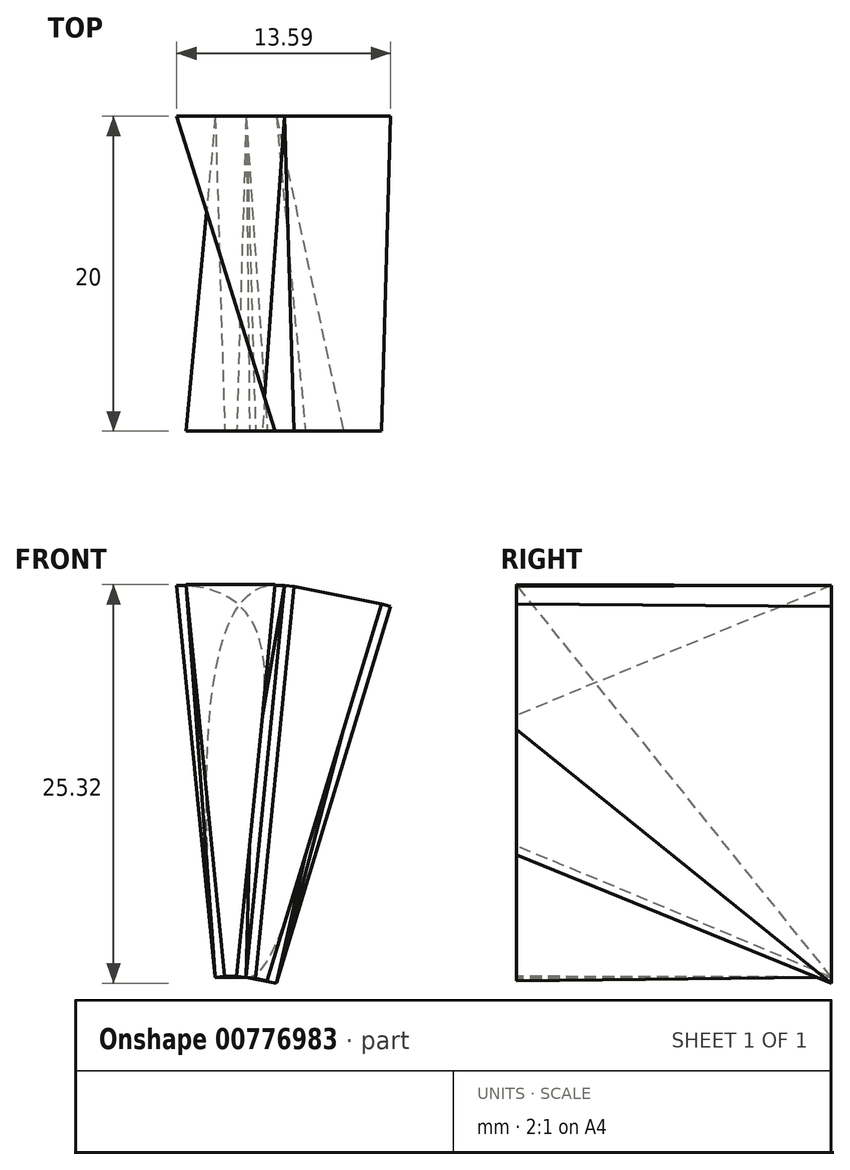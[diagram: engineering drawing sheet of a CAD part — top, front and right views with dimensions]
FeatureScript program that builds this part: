
annotation { "Feature Type Name" : "Feature", "Feature Type Description" : "" }
export const myFeature = defineFeature(function(context is Context, id is Id, definition is map)
    precondition{}
    {
        {
            var Q0;
            Q0=qCreatedBy(makeId("Front.planeOp"),FACE);
            var sketch = newSketch(context, id + "F0", { "sketchPlane" : qUnion([Q0])});
            skCircle(sketch, "E0", {"center": v(0, 0) * mm, "radius": 10 * mm, "construction": true});
            skCircle(sketch, "E1", {"center": v(0, 0) * mm, "radius": 35 * mm, "construction": true});
            skCircle(sketch, "E2", {"center": v(0, 0) * mm, "radius": 49 * mm});
            skLineSegment(sketch, "E3", {"start": v(-0.98, 9.95) * mm, "end": v(0.98, 9.95) * mm});
            skLineSegment(sketch, "E4", {"start": v(0.98, 9.95) * mm, "end": v(3.43, 34.83) * mm});
            skLineSegment(sketch, "E5", {"start": v(3.43, 34.83) * mm, "end": v(-3.43, 34.83) * mm});
            skLineSegment(sketch, "E6", {"start": v(-3.43, 34.83) * mm, "end": v(-0.98, 9.95) * mm});
            skLineSegment(sketch, "E7", {"start": v(0, 0) * mm, "end": v(-4.8, 48.76) * mm, "construction": true});
            skLineSegment(sketch, "E8", {"start": v(-4.8, 48.76) * mm, "end": v(0, 0) * mm, "construction": true});
            skLineSegment(sketch, "E9", {"start": v(0, 0) * mm, "end": v(4.8, 48.76) * mm, "construction": true});
            skLineSegment(sketch, "E10.1.0", {"start": v(-10.16, 33.5) * mm, "end": v(-2.9, 9.57) * mm});
            skLineSegment(sketch, "E10.1.1", {"start": v(-3.43, 34.83) * mm, "end": v(-10.16, 33.5) * mm});
            skLineSegment(sketch, "E10.1.2", {"start": v(-0.98, 9.95) * mm, "end": v(-3.43, 34.83) * mm});
            skLineSegment(sketch, "E10.1.3", {"start": v(-2.9, 9.57) * mm, "end": v(-0.98, 9.95) * mm});
            skLineSegment(sketch, "E10.2.0", {"start": v(-16.5, 30.87) * mm, "end": v(-4.72, 8.82) * mm});
            skLineSegment(sketch, "E10.2.1", {"start": v(-10.16, 33.5) * mm, "end": v(-16.5, 30.87) * mm});
            skLineSegment(sketch, "E10.2.2", {"start": v(-2.9, 9.57) * mm, "end": v(-10.16, 33.5) * mm});
            skLineSegment(sketch, "E10.2.3", {"start": v(-4.72, 8.82) * mm, "end": v(-2.9, 9.57) * mm});
            skLineSegment(sketch, "E10.3.0", {"start": v(-22.2, 27.05) * mm, "end": v(-6.35, 7.73) * mm});
            skLineSegment(sketch, "E10.3.1", {"start": v(-16.5, 30.87) * mm, "end": v(-22.2, 27.05) * mm});
            skLineSegment(sketch, "E10.3.2", {"start": v(-4.71, 8.82) * mm, "end": v(-16.5, 30.87) * mm});
            skLineSegment(sketch, "E10.3.3", {"start": v(-6.35, 7.73) * mm, "end": v(-4.71, 8.82) * mm});
            skLineSegment(sketch, "E10.4.0", {"start": v(-27.06, 22.2) * mm, "end": v(-7.73, 6.34) * mm});
            skLineSegment(sketch, "E10.4.1", {"start": v(-22.2, 27.06) * mm, "end": v(-27.06, 22.2) * mm});
            skLineSegment(sketch, "E10.4.2", {"start": v(-6.34, 7.73) * mm, "end": v(-22.2, 27.06) * mm});
            skLineSegment(sketch, "E10.4.3", {"start": v(-7.73, 6.34) * mm, "end": v(-6.34, 7.73) * mm});
            skLineSegment(sketch, "E10.5.0", {"start": v(-30.87, 16.5) * mm, "end": v(-8.82, 4.71) * mm});
            skLineSegment(sketch, "E10.5.1", {"start": v(-27.05, 22.2) * mm, "end": v(-30.87, 16.5) * mm});
            skLineSegment(sketch, "E10.5.2", {"start": v(-7.73, 6.35) * mm, "end": v(-27.05, 22.2) * mm});
            skLineSegment(sketch, "E10.5.3", {"start": v(-8.82, 4.71) * mm, "end": v(-7.73, 6.35) * mm});
            skLineSegment(sketch, "E10.6.0", {"start": v(-33.5, 10.16) * mm, "end": v(-9.57, 2.9) * mm});
            skLineSegment(sketch, "E10.6.1", {"start": v(-30.87, 16.5) * mm, "end": v(-33.5, 10.16) * mm});
            skLineSegment(sketch, "E10.6.2", {"start": v(-8.82, 4.72) * mm, "end": v(-30.87, 16.5) * mm});
            skLineSegment(sketch, "E10.6.3", {"start": v(-9.57, 2.9) * mm, "end": v(-8.82, 4.72) * mm});
            skLineSegment(sketch, "E10.7.0", {"start": v(-34.83, 3.43) * mm, "end": v(-9.95, 0.98) * mm});
            skLineSegment(sketch, "E10.7.1", {"start": v(-33.5, 10.16) * mm, "end": v(-34.83, 3.43) * mm});
            skLineSegment(sketch, "E10.7.2", {"start": v(-9.57, 2.9) * mm, "end": v(-33.5, 10.16) * mm});
            skLineSegment(sketch, "E10.7.3", {"start": v(-9.95, 0.98) * mm, "end": v(-9.57, 2.9) * mm});
            skLineSegment(sketch, "E10.8.0", {"start": v(-34.83, -3.43) * mm, "end": v(-9.95, -0.98) * mm});
            skLineSegment(sketch, "E10.8.1", {"start": v(-34.83, 3.43) * mm, "end": v(-34.83, -3.43) * mm});
            skLineSegment(sketch, "E10.8.2", {"start": v(-9.95, 0.98) * mm, "end": v(-34.83, 3.43) * mm});
            skLineSegment(sketch, "E10.8.3", {"start": v(-9.95, -0.98) * mm, "end": v(-9.95, 0.98) * mm});
            skLineSegment(sketch, "E10.9.0", {"start": v(-33.5, -10.16) * mm, "end": v(-9.57, -2.9) * mm});
            skLineSegment(sketch, "E10.9.1", {"start": v(-34.83, -3.43) * mm, "end": v(-33.5, -10.16) * mm});
            skLineSegment(sketch, "E10.9.2", {"start": v(-9.95, -0.98) * mm, "end": v(-34.83, -3.43) * mm});
            skLineSegment(sketch, "E10.9.3", {"start": v(-9.57, -2.9) * mm, "end": v(-9.95, -0.98) * mm});
            skLineSegment(sketch, "E10.10.0", {"start": v(-30.87, -16.5) * mm, "end": v(-8.82, -4.72) * mm});
            skLineSegment(sketch, "E10.10.1", {"start": v(-33.5, -10.16) * mm, "end": v(-30.87, -16.5) * mm});
            skLineSegment(sketch, "E10.10.2", {"start": v(-9.57, -2.9) * mm, "end": v(-33.5, -10.16) * mm});
            skLineSegment(sketch, "E10.10.3", {"start": v(-8.82, -4.72) * mm, "end": v(-9.57, -2.9) * mm});
            skLineSegment(sketch, "E10.11.0", {"start": v(-27.05, -22.2) * mm, "end": v(-7.73, -6.35) * mm});
            skLineSegment(sketch, "E10.11.1", {"start": v(-30.87, -16.5) * mm, "end": v(-27.05, -22.2) * mm});
            skLineSegment(sketch, "E10.11.2", {"start": v(-8.82, -4.71) * mm, "end": v(-30.87, -16.5) * mm});
            skLineSegment(sketch, "E10.11.3", {"start": v(-7.73, -6.35) * mm, "end": v(-8.82, -4.71) * mm});
            skLineSegment(sketch, "E10.12.0", {"start": v(-22.2, -27.06) * mm, "end": v(-6.34, -7.73) * mm});
            skLineSegment(sketch, "E10.12.1", {"start": v(-27.06, -22.2) * mm, "end": v(-22.2, -27.06) * mm});
            skLineSegment(sketch, "E10.12.2", {"start": v(-7.73, -6.34) * mm, "end": v(-27.06, -22.2) * mm});
            skLineSegment(sketch, "E10.12.3", {"start": v(-6.34, -7.73) * mm, "end": v(-7.73, -6.34) * mm});
            skLineSegment(sketch, "E10.13.0", {"start": v(-16.5, -30.87) * mm, "end": v(-4.71, -8.82) * mm});
            skLineSegment(sketch, "E10.13.1", {"start": v(-22.2, -27.05) * mm, "end": v(-16.5, -30.87) * mm});
            skLineSegment(sketch, "E10.13.2", {"start": v(-6.35, -7.73) * mm, "end": v(-22.2, -27.05) * mm});
            skLineSegment(sketch, "E10.13.3", {"start": v(-4.71, -8.82) * mm, "end": v(-6.35, -7.73) * mm});
            skLineSegment(sketch, "E10.14.0", {"start": v(-10.16, -33.5) * mm, "end": v(-2.9, -9.57) * mm});
            skLineSegment(sketch, "E10.14.1", {"start": v(-16.5, -30.87) * mm, "end": v(-10.16, -33.5) * mm});
            skLineSegment(sketch, "E10.14.2", {"start": v(-4.72, -8.82) * mm, "end": v(-16.5, -30.87) * mm});
            skLineSegment(sketch, "E10.14.3", {"start": v(-2.9, -9.57) * mm, "end": v(-4.72, -8.82) * mm});
            skLineSegment(sketch, "E10.15.0", {"start": v(-3.43, -34.83) * mm, "end": v(-0.98, -9.95) * mm});
            skLineSegment(sketch, "E10.15.1", {"start": v(-10.16, -33.5) * mm, "end": v(-3.43, -34.83) * mm});
            skLineSegment(sketch, "E10.15.2", {"start": v(-2.9, -9.57) * mm, "end": v(-10.16, -33.5) * mm});
            skLineSegment(sketch, "E10.15.3", {"start": v(-0.98, -9.95) * mm, "end": v(-2.9, -9.57) * mm});
            skLineSegment(sketch, "E10.16.0", {"start": v(3.43, -34.83) * mm, "end": v(0.98, -9.95) * mm});
            skLineSegment(sketch, "E10.16.1", {"start": v(-3.43, -34.83) * mm, "end": v(3.43, -34.83) * mm});
            skLineSegment(sketch, "E10.16.2", {"start": v(-0.98, -9.95) * mm, "end": v(-3.43, -34.83) * mm});
            skLineSegment(sketch, "E10.16.3", {"start": v(0.98, -9.95) * mm, "end": v(-0.98, -9.95) * mm});
            skLineSegment(sketch, "E10.17.0", {"start": v(10.16, -33.5) * mm, "end": v(2.9, -9.57) * mm});
            skLineSegment(sketch, "E10.17.1", {"start": v(3.43, -34.83) * mm, "end": v(10.16, -33.5) * mm});
            skLineSegment(sketch, "E10.17.2", {"start": v(0.98, -9.95) * mm, "end": v(3.43, -34.83) * mm});
            skLineSegment(sketch, "E10.17.3", {"start": v(2.9, -9.57) * mm, "end": v(0.98, -9.95) * mm});
            skLineSegment(sketch, "E10.18.0", {"start": v(16.5, -30.87) * mm, "end": v(4.72, -8.82) * mm});
            skLineSegment(sketch, "E10.18.1", {"start": v(10.16, -33.5) * mm, "end": v(16.5, -30.87) * mm});
            skLineSegment(sketch, "E10.18.2", {"start": v(2.9, -9.57) * mm, "end": v(10.16, -33.5) * mm});
            skLineSegment(sketch, "E10.18.3", {"start": v(4.72, -8.82) * mm, "end": v(2.9, -9.57) * mm});
            skLineSegment(sketch, "E10.19.0", {"start": v(22.2, -27.05) * mm, "end": v(6.35, -7.73) * mm});
            skLineSegment(sketch, "E10.19.1", {"start": v(16.5, -30.87) * mm, "end": v(22.2, -27.05) * mm});
            skLineSegment(sketch, "E10.19.2", {"start": v(4.71, -8.82) * mm, "end": v(16.5, -30.87) * mm});
            skLineSegment(sketch, "E10.19.3", {"start": v(6.35, -7.73) * mm, "end": v(4.71, -8.82) * mm});
            skLineSegment(sketch, "E10.20.0", {"start": v(27.06, -22.2) * mm, "end": v(7.73, -6.34) * mm});
            skLineSegment(sketch, "E10.20.1", {"start": v(22.2, -27.06) * mm, "end": v(27.06, -22.2) * mm});
            skLineSegment(sketch, "E10.20.2", {"start": v(6.34, -7.73) * mm, "end": v(22.2, -27.06) * mm});
            skLineSegment(sketch, "E10.20.3", {"start": v(7.73, -6.34) * mm, "end": v(6.34, -7.73) * mm});
            skLineSegment(sketch, "E10.21.0", {"start": v(30.87, -16.5) * mm, "end": v(8.82, -4.71) * mm});
            skLineSegment(sketch, "E10.21.1", {"start": v(27.05, -22.2) * mm, "end": v(30.87, -16.5) * mm});
            skLineSegment(sketch, "E10.21.2", {"start": v(7.73, -6.35) * mm, "end": v(27.05, -22.2) * mm});
            skLineSegment(sketch, "E10.21.3", {"start": v(8.82, -4.71) * mm, "end": v(7.73, -6.35) * mm});
            skLineSegment(sketch, "E10.22.1", {"start": v(30.87, -16.5) * mm, "end": v(33.5, -10.16) * mm});
            skLineSegment(sketch, "E10.22.2", {"start": v(8.82, -4.72) * mm, "end": v(30.87, -16.5) * mm});
            skLineSegment(sketch, "E10.22.3", {"start": v(9.57, -2.9) * mm, "end": v(8.82, -4.72) * mm});
            skLineSegment(sketch, "E10.23.0", {"start": v(34.83, -3.43) * mm, "end": v(9.95, -0.98) * mm});
            skLineSegment(sketch, "E10.23.1", {"start": v(33.5, -10.16) * mm, "end": v(34.83, -3.43) * mm});
            skLineSegment(sketch, "E10.23.3", {"start": v(9.95, -0.98) * mm, "end": v(9.57, -2.9) * mm});
            skLineSegment(sketch, "E10.24.0", {"start": v(34.83, 3.43) * mm, "end": v(9.95, 0.98) * mm});
            skLineSegment(sketch, "E10.24.1", {"start": v(34.83, -3.43) * mm, "end": v(34.83, 3.43) * mm});
            skLineSegment(sketch, "E10.24.2", {"start": v(9.95, -0.98) * mm, "end": v(34.83, -3.43) * mm});
            skLineSegment(sketch, "E10.24.3", {"start": v(9.95, 0.98) * mm, "end": v(9.95, -0.98) * mm});
            skLineSegment(sketch, "E10.25.0", {"start": v(33.5, 10.16) * mm, "end": v(9.57, 2.9) * mm});
            skLineSegment(sketch, "E10.25.1", {"start": v(34.83, 3.43) * mm, "end": v(33.5, 10.16) * mm});
            skLineSegment(sketch, "E10.25.2", {"start": v(9.95, 0.98) * mm, "end": v(34.83, 3.43) * mm});
            skLineSegment(sketch, "E10.25.3", {"start": v(9.57, 2.9) * mm, "end": v(9.95, 0.98) * mm});
            skLineSegment(sketch, "E10.26.0", {"start": v(30.87, 16.5) * mm, "end": v(8.82, 4.72) * mm});
            skLineSegment(sketch, "E10.26.1", {"start": v(33.5, 10.16) * mm, "end": v(30.87, 16.5) * mm});
            skLineSegment(sketch, "E10.26.2", {"start": v(9.57, 2.9) * mm, "end": v(33.5, 10.16) * mm});
            skLineSegment(sketch, "E10.26.3", {"start": v(8.82, 4.72) * mm, "end": v(9.57, 2.9) * mm});
            skLineSegment(sketch, "E10.27.0", {"start": v(27.05, 22.2) * mm, "end": v(7.73, 6.35) * mm});
            skLineSegment(sketch, "E10.27.1", {"start": v(30.87, 16.5) * mm, "end": v(27.05, 22.2) * mm});
            skLineSegment(sketch, "E10.27.2", {"start": v(8.82, 4.71) * mm, "end": v(30.87, 16.5) * mm});
            skLineSegment(sketch, "E10.27.3", {"start": v(7.73, 6.35) * mm, "end": v(8.82, 4.71) * mm});
            skLineSegment(sketch, "E10.28.0", {"start": v(22.2, 27.06) * mm, "end": v(6.34, 7.73) * mm});
            skLineSegment(sketch, "E10.28.1", {"start": v(27.06, 22.2) * mm, "end": v(22.2, 27.06) * mm});
            skLineSegment(sketch, "E10.28.2", {"start": v(7.73, 6.34) * mm, "end": v(27.06, 22.2) * mm});
            skLineSegment(sketch, "E10.28.3", {"start": v(6.34, 7.73) * mm, "end": v(7.73, 6.34) * mm});
            skLineSegment(sketch, "E10.29.0", {"start": v(16.5, 30.87) * mm, "end": v(4.71, 8.82) * mm});
            skLineSegment(sketch, "E10.29.1", {"start": v(22.2, 27.05) * mm, "end": v(16.5, 30.87) * mm});
            skLineSegment(sketch, "E10.29.2", {"start": v(6.35, 7.73) * mm, "end": v(22.2, 27.05) * mm});
            skLineSegment(sketch, "E10.29.3", {"start": v(4.71, 8.82) * mm, "end": v(6.35, 7.73) * mm});
            skLineSegment(sketch, "E10.30.0", {"start": v(10.16, 33.5) * mm, "end": v(2.9, 9.57) * mm});
            skLineSegment(sketch, "E10.30.1", {"start": v(16.5, 30.87) * mm, "end": v(10.16, 33.5) * mm});
            skLineSegment(sketch, "E10.30.2", {"start": v(4.72, 8.82) * mm, "end": v(16.5, 30.87) * mm});
            skLineSegment(sketch, "E10.30.3", {"start": v(2.9, 9.57) * mm, "end": v(4.72, 8.82) * mm});
            skLineSegment(sketch, "E10.31.0", {"start": v(3.43, 34.83) * mm, "end": v(0.98, 9.95) * mm});
            skLineSegment(sketch, "E10.31.1", {"start": v(10.16, 33.5) * mm, "end": v(3.43, 34.83) * mm});
            skLineSegment(sketch, "E10.31.2", {"start": v(2.9, 9.57) * mm, "end": v(10.16, 33.5) * mm});
            skLineSegment(sketch, "E10.31.3", {"start": v(0.98, 9.95) * mm, "end": v(2.9, 9.57) * mm});
            skLineSegment(sketch, "E11", {"start": v(9.57, -2.9) * mm, "end": v(33.5, -10.16) * mm});
            skSolve(sketch);
        }
        {
            var Q0;
            Q0=qCreatedBy(makeId("Front.planeOp"),FACE);
            cPlane(context, id + "F1", {"entities" : qUnion([Q0]), "cplaneType" : CPlaneType.OFFSET, "offset" : 200 * mm, "width" : 150 * mm, "height" : 150 * mm});
        }
        {
            var Q0;
            Q0=qCreatedBy(makeId("Front.planeOp"),FACE);
            cPlane(context, id + "F2", {"entities" : qUnion([Q0]), "cplaneType" : CPlaneType.OFFSET, "offset" : 20 * mm, "width" : 150 * mm, "height" : 150 * mm});
        }
        {
            var Q0;
            Q0=qCreatedBy(id+"F2.planeOp",FACE);
            var sketch = newSketch(context, id + "F3", { "sketchPlane" : qUnion([Q0])});
            skLineSegment(sketch, "E12", {"start": v(2.83, 34.89) * mm, "end": v(-2.83, 34.89) * mm});
            skLineSegment(sketch, "E13", {"start": v(-2.83, 34.89) * mm, "end": v(-0.38, 10) * mm});
            skLineSegment(sketch, "E14", {"start": v(-0.38, 10) * mm, "end": v(0.38, 10) * mm});
            skLineSegment(sketch, "E15", {"start": v(0.38, 10) * mm, "end": v(2.83, 34.89) * mm});
            skLineSegment(sketch, "E16.1.0", {"start": v(-9.58, 33.66) * mm, "end": v(-2.32, 9.73) * mm});
            skLineSegment(sketch, "E16.1.1", {"start": v(-4.03, 34.77) * mm, "end": v(-9.58, 33.66) * mm});
            skLineSegment(sketch, "E16.1.2", {"start": v(-1.58, 9.88) * mm, "end": v(-4.03, 34.77) * mm});
            skLineSegment(sketch, "E16.1.3", {"start": v(-2.32, 9.73) * mm, "end": v(-1.58, 9.88) * mm});
            skLineSegment(sketch, "E16.2.0", {"start": v(-15.96, 31.15) * mm, "end": v(-4.18, 9.1) * mm});
            skLineSegment(sketch, "E16.2.1", {"start": v(-10.74, 33.31) * mm, "end": v(-15.96, 31.15) * mm});
            skLineSegment(sketch, "E16.2.2", {"start": v(-3.48, 9.38) * mm, "end": v(-10.74, 33.31) * mm});
            skLineSegment(sketch, "E16.2.3", {"start": v(-4.18, 9.1) * mm, "end": v(-3.48, 9.38) * mm});
            skLineSegment(sketch, "E16.3.0", {"start": v(-21.73, 27.43) * mm, "end": v(-5.87, 8.1) * mm});
            skLineSegment(sketch, "E16.3.1", {"start": v(-17.03, 30.58) * mm, "end": v(-21.73, 27.43) * mm});
            skLineSegment(sketch, "E16.3.2", {"start": v(-5.24, 8.53) * mm, "end": v(-17.03, 30.58) * mm});
            skLineSegment(sketch, "E16.3.3", {"start": v(-5.87, 8.1) * mm, "end": v(-5.24, 8.53) * mm});
            skLineSegment(sketch, "E16.4.0", {"start": v(-26.67, 22.67) * mm, "end": v(-7.34, 6.8) * mm});
            skLineSegment(sketch, "E16.4.1", {"start": v(-22.67, 26.67) * mm, "end": v(-26.67, 22.67) * mm});
            skLineSegment(sketch, "E16.4.2", {"start": v(-6.8, 7.34) * mm, "end": v(-22.67, 26.67) * mm});
            skLineSegment(sketch, "E16.4.3", {"start": v(-7.34, 6.8) * mm, "end": v(-6.8, 7.34) * mm});
            skLineSegment(sketch, "E16.5.0", {"start": v(-30.58, 17.03) * mm, "end": v(-8.53, 5.24) * mm});
            skLineSegment(sketch, "E16.5.1", {"start": v(-27.43, 21.73) * mm, "end": v(-30.58, 17.03) * mm});
            skLineSegment(sketch, "E16.5.2", {"start": v(-8.1, 5.87) * mm, "end": v(-27.43, 21.73) * mm});
            skLineSegment(sketch, "E16.5.3", {"start": v(-8.53, 5.24) * mm, "end": v(-8.1, 5.87) * mm});
            skLineSegment(sketch, "E16.6.0", {"start": v(-33.31, 10.74) * mm, "end": v(-9.38, 3.48) * mm});
            skLineSegment(sketch, "E16.6.1", {"start": v(-31.15, 15.96) * mm, "end": v(-33.31, 10.74) * mm});
            skLineSegment(sketch, "E16.6.2", {"start": v(-9.1, 4.18) * mm, "end": v(-31.15, 15.96) * mm});
            skLineSegment(sketch, "E16.6.3", {"start": v(-9.38, 3.48) * mm, "end": v(-9.1, 4.18) * mm});
            skLineSegment(sketch, "E16.7.0", {"start": v(-34.77, 4.03) * mm, "end": v(-9.88, 1.58) * mm});
            skLineSegment(sketch, "E16.7.1", {"start": v(-33.66, 9.58) * mm, "end": v(-34.77, 4.03) * mm});
            skLineSegment(sketch, "E16.7.2", {"start": v(-9.73, 2.32) * mm, "end": v(-33.66, 9.58) * mm});
            skLineSegment(sketch, "E16.7.3", {"start": v(-9.88, 1.58) * mm, "end": v(-9.73, 2.32) * mm});
            skLineSegment(sketch, "E16.8.0", {"start": v(-34.89, -2.83) * mm, "end": v(-10, -0.38) * mm});
            skLineSegment(sketch, "E16.8.1", {"start": v(-34.89, 2.83) * mm, "end": v(-34.89, -2.83) * mm});
            skLineSegment(sketch, "E16.8.2", {"start": v(-10, 0.38) * mm, "end": v(-34.89, 2.83) * mm});
            skLineSegment(sketch, "E16.8.3", {"start": v(-10, -0.38) * mm, "end": v(-10, 0.38) * mm});
            skLineSegment(sketch, "E16.9.0", {"start": v(-33.66, -9.58) * mm, "end": v(-9.73, -2.32) * mm});
            skLineSegment(sketch, "E16.9.1", {"start": v(-34.77, -4.03) * mm, "end": v(-33.66, -9.58) * mm});
            skLineSegment(sketch, "E16.9.2", {"start": v(-9.88, -1.58) * mm, "end": v(-34.77, -4.03) * mm});
            skLineSegment(sketch, "E16.9.3", {"start": v(-9.73, -2.32) * mm, "end": v(-9.88, -1.58) * mm});
            skLineSegment(sketch, "E16.10.0", {"start": v(-31.15, -15.96) * mm, "end": v(-9.1, -4.18) * mm});
            skLineSegment(sketch, "E16.10.1", {"start": v(-33.31, -10.74) * mm, "end": v(-31.15, -15.96) * mm});
            skLineSegment(sketch, "E16.10.2", {"start": v(-9.38, -3.48) * mm, "end": v(-33.31, -10.74) * mm});
            skLineSegment(sketch, "E16.10.3", {"start": v(-9.1, -4.18) * mm, "end": v(-9.38, -3.48) * mm});
            skLineSegment(sketch, "E16.11.0", {"start": v(-27.43, -21.73) * mm, "end": v(-8.1, -5.87) * mm});
            skLineSegment(sketch, "E16.11.1", {"start": v(-30.58, -17.03) * mm, "end": v(-27.43, -21.73) * mm});
            skLineSegment(sketch, "E16.11.2", {"start": v(-8.53, -5.24) * mm, "end": v(-30.58, -17.03) * mm});
            skLineSegment(sketch, "E16.11.3", {"start": v(-8.1, -5.87) * mm, "end": v(-8.53, -5.24) * mm});
            skLineSegment(sketch, "E16.12.0", {"start": v(-22.67, -26.67) * mm, "end": v(-6.8, -7.34) * mm});
            skLineSegment(sketch, "E16.12.1", {"start": v(-26.67, -22.67) * mm, "end": v(-22.67, -26.67) * mm});
            skLineSegment(sketch, "E16.12.2", {"start": v(-7.34, -6.8) * mm, "end": v(-26.67, -22.67) * mm});
            skLineSegment(sketch, "E16.12.3", {"start": v(-6.8, -7.34) * mm, "end": v(-7.34, -6.8) * mm});
            skLineSegment(sketch, "E16.13.0", {"start": v(-17.03, -30.58) * mm, "end": v(-5.24, -8.53) * mm});
            skLineSegment(sketch, "E16.13.1", {"start": v(-21.73, -27.43) * mm, "end": v(-17.03, -30.58) * mm});
            skLineSegment(sketch, "E16.13.2", {"start": v(-5.87, -8.1) * mm, "end": v(-21.73, -27.43) * mm});
            skLineSegment(sketch, "E16.13.3", {"start": v(-5.24, -8.53) * mm, "end": v(-5.87, -8.1) * mm});
            skLineSegment(sketch, "E16.14.0", {"start": v(-10.74, -33.31) * mm, "end": v(-3.48, -9.38) * mm});
            skLineSegment(sketch, "E16.14.1", {"start": v(-15.96, -31.15) * mm, "end": v(-10.74, -33.31) * mm});
            skLineSegment(sketch, "E16.14.2", {"start": v(-4.18, -9.1) * mm, "end": v(-15.96, -31.15) * mm});
            skLineSegment(sketch, "E16.14.3", {"start": v(-3.48, -9.38) * mm, "end": v(-4.18, -9.1) * mm});
            skLineSegment(sketch, "E16.15.0", {"start": v(-4.03, -34.77) * mm, "end": v(-1.58, -9.88) * mm});
            skLineSegment(sketch, "E16.15.1", {"start": v(-9.58, -33.66) * mm, "end": v(-4.03, -34.77) * mm});
            skLineSegment(sketch, "E16.15.2", {"start": v(-2.32, -9.73) * mm, "end": v(-9.58, -33.66) * mm});
            skLineSegment(sketch, "E16.15.3", {"start": v(-1.58, -9.88) * mm, "end": v(-2.32, -9.73) * mm});
            skLineSegment(sketch, "E16.16.0", {"start": v(2.83, -34.89) * mm, "end": v(0.38, -10) * mm});
            skLineSegment(sketch, "E16.16.1", {"start": v(-2.83, -34.89) * mm, "end": v(2.83, -34.89) * mm});
            skLineSegment(sketch, "E16.16.2", {"start": v(-0.38, -10) * mm, "end": v(-2.83, -34.89) * mm});
            skLineSegment(sketch, "E16.16.3", {"start": v(0.38, -10) * mm, "end": v(-0.38, -10) * mm});
            skLineSegment(sketch, "E16.17.0", {"start": v(9.58, -33.66) * mm, "end": v(2.32, -9.73) * mm});
            skLineSegment(sketch, "E16.17.1", {"start": v(4.03, -34.77) * mm, "end": v(9.58, -33.66) * mm});
            skLineSegment(sketch, "E16.17.2", {"start": v(1.58, -9.88) * mm, "end": v(4.03, -34.77) * mm});
            skLineSegment(sketch, "E16.17.3", {"start": v(2.32, -9.73) * mm, "end": v(1.58, -9.88) * mm});
            skLineSegment(sketch, "E16.18.0", {"start": v(15.96, -31.15) * mm, "end": v(4.18, -9.1) * mm});
            skLineSegment(sketch, "E16.18.1", {"start": v(10.74, -33.31) * mm, "end": v(15.96, -31.15) * mm});
            skLineSegment(sketch, "E16.18.2", {"start": v(3.48, -9.38) * mm, "end": v(10.74, -33.31) * mm});
            skLineSegment(sketch, "E16.18.3", {"start": v(4.18, -9.1) * mm, "end": v(3.48, -9.38) * mm});
            skLineSegment(sketch, "E16.19.0", {"start": v(21.73, -27.43) * mm, "end": v(5.87, -8.1) * mm});
            skLineSegment(sketch, "E16.19.1", {"start": v(17.03, -30.58) * mm, "end": v(21.73, -27.43) * mm});
            skLineSegment(sketch, "E16.19.2", {"start": v(5.24, -8.53) * mm, "end": v(17.03, -30.58) * mm});
            skLineSegment(sketch, "E16.19.3", {"start": v(5.87, -8.1) * mm, "end": v(5.24, -8.53) * mm});
            skLineSegment(sketch, "E16.20.0", {"start": v(26.67, -22.67) * mm, "end": v(7.34, -6.8) * mm});
            skLineSegment(sketch, "E16.20.1", {"start": v(22.67, -26.67) * mm, "end": v(26.67, -22.67) * mm});
            skLineSegment(sketch, "E16.20.2", {"start": v(6.8, -7.34) * mm, "end": v(22.67, -26.67) * mm});
            skLineSegment(sketch, "E16.20.3", {"start": v(7.34, -6.8) * mm, "end": v(6.8, -7.34) * mm});
            skLineSegment(sketch, "E16.21.0", {"start": v(30.58, -17.03) * mm, "end": v(8.53, -5.24) * mm});
            skLineSegment(sketch, "E16.21.1", {"start": v(27.43, -21.73) * mm, "end": v(30.58, -17.03) * mm});
            skLineSegment(sketch, "E16.21.2", {"start": v(8.1, -5.87) * mm, "end": v(27.43, -21.73) * mm});
            skLineSegment(sketch, "E16.21.3", {"start": v(8.53, -5.24) * mm, "end": v(8.1, -5.87) * mm});
            skLineSegment(sketch, "E16.22.0", {"start": v(33.31, -10.74) * mm, "end": v(9.38, -3.48) * mm});
            skLineSegment(sketch, "E16.22.1", {"start": v(31.15, -15.96) * mm, "end": v(33.31, -10.74) * mm});
            skLineSegment(sketch, "E16.22.2", {"start": v(9.1, -4.18) * mm, "end": v(31.15, -15.96) * mm});
            skLineSegment(sketch, "E16.22.3", {"start": v(9.38, -3.48) * mm, "end": v(9.1, -4.18) * mm});
            skLineSegment(sketch, "E16.23.0", {"start": v(34.77, -4.03) * mm, "end": v(9.88, -1.58) * mm});
            skLineSegment(sketch, "E16.23.1", {"start": v(33.66, -9.58) * mm, "end": v(34.77, -4.03) * mm});
            skLineSegment(sketch, "E16.23.2", {"start": v(9.73, -2.32) * mm, "end": v(33.66, -9.58) * mm});
            skLineSegment(sketch, "E16.23.3", {"start": v(9.88, -1.58) * mm, "end": v(9.73, -2.32) * mm});
            skLineSegment(sketch, "E16.24.0", {"start": v(34.89, 2.83) * mm, "end": v(10, 0.38) * mm});
            skLineSegment(sketch, "E16.24.1", {"start": v(34.89, -2.83) * mm, "end": v(34.89, 2.83) * mm});
            skLineSegment(sketch, "E16.24.2", {"start": v(10, -0.38) * mm, "end": v(34.89, -2.83) * mm});
            skLineSegment(sketch, "E16.24.3", {"start": v(10, 0.38) * mm, "end": v(10, -0.38) * mm});
            skLineSegment(sketch, "E16.25.0", {"start": v(33.66, 9.58) * mm, "end": v(9.73, 2.32) * mm});
            skLineSegment(sketch, "E16.25.1", {"start": v(34.77, 4.03) * mm, "end": v(33.66, 9.58) * mm});
            skLineSegment(sketch, "E16.25.2", {"start": v(9.88, 1.58) * mm, "end": v(34.77, 4.03) * mm});
            skLineSegment(sketch, "E16.25.3", {"start": v(9.73, 2.32) * mm, "end": v(9.88, 1.58) * mm});
            skLineSegment(sketch, "E16.26.0", {"start": v(31.15, 15.96) * mm, "end": v(9.1, 4.18) * mm});
            skLineSegment(sketch, "E16.26.1", {"start": v(33.31, 10.74) * mm, "end": v(31.15, 15.96) * mm});
            skLineSegment(sketch, "E16.26.2", {"start": v(9.38, 3.48) * mm, "end": v(33.31, 10.74) * mm});
            skLineSegment(sketch, "E16.26.3", {"start": v(9.1, 4.18) * mm, "end": v(9.38, 3.48) * mm});
            skLineSegment(sketch, "E16.27.0", {"start": v(27.43, 21.73) * mm, "end": v(8.1, 5.87) * mm});
            skLineSegment(sketch, "E16.27.1", {"start": v(30.58, 17.03) * mm, "end": v(27.43, 21.73) * mm});
            skLineSegment(sketch, "E16.27.2", {"start": v(8.53, 5.24) * mm, "end": v(30.58, 17.03) * mm});
            skLineSegment(sketch, "E16.27.3", {"start": v(8.1, 5.87) * mm, "end": v(8.53, 5.24) * mm});
            skLineSegment(sketch, "E16.28.0", {"start": v(22.67, 26.67) * mm, "end": v(6.8, 7.34) * mm});
            skLineSegment(sketch, "E16.28.1", {"start": v(26.67, 22.67) * mm, "end": v(22.67, 26.67) * mm});
            skLineSegment(sketch, "E16.28.2", {"start": v(7.34, 6.8) * mm, "end": v(26.67, 22.67) * mm});
            skLineSegment(sketch, "E16.28.3", {"start": v(6.8, 7.34) * mm, "end": v(7.34, 6.8) * mm});
            skLineSegment(sketch, "E16.29.0", {"start": v(17.03, 30.58) * mm, "end": v(5.24, 8.53) * mm});
            skLineSegment(sketch, "E16.29.1", {"start": v(21.73, 27.43) * mm, "end": v(17.03, 30.58) * mm});
            skLineSegment(sketch, "E16.29.2", {"start": v(5.87, 8.1) * mm, "end": v(21.73, 27.43) * mm});
            skLineSegment(sketch, "E16.29.3", {"start": v(5.24, 8.53) * mm, "end": v(5.87, 8.1) * mm});
            skLineSegment(sketch, "E16.30.0", {"start": v(10.74, 33.31) * mm, "end": v(3.48, 9.38) * mm});
            skLineSegment(sketch, "E16.30.1", {"start": v(15.96, 31.15) * mm, "end": v(10.74, 33.31) * mm});
            skLineSegment(sketch, "E16.30.2", {"start": v(4.18, 9.1) * mm, "end": v(15.96, 31.15) * mm});
            skLineSegment(sketch, "E16.30.3", {"start": v(3.48, 9.38) * mm, "end": v(4.18, 9.1) * mm});
            skLineSegment(sketch, "E16.31.0", {"start": v(4.03, 34.77) * mm, "end": v(1.58, 9.88) * mm});
            skLineSegment(sketch, "E16.31.1", {"start": v(9.58, 33.66) * mm, "end": v(4.03, 34.77) * mm});
            skLineSegment(sketch, "E16.31.2", {"start": v(2.32, 9.73) * mm, "end": v(9.58, 33.66) * mm});
            skLineSegment(sketch, "E16.31.3", {"start": v(1.58, 9.88) * mm, "end": v(2.32, 9.73) * mm});
            skPoint(sketch, "E16.center", {"position": v(0, 0) * mm});
            skSolve(sketch);
        }
        {
            var Q0;
            {var subQ0=sQuery(id+"F0.wireOp",EDGE,"E10.1.3");var subQ3=sQuery(id+"F0.wireOp",EDGE,"E3");var subQ4=makeQuery(id+"F0.imprint","INTERSECT",VERTEX,{"derivedFrom":[subQ3,subQ0]});Q0=makeQuery(id+"F0.imprint","IMPRINT",FACE,{"disambiguationData":[TD([[makeQuery(id+"F0.imprint","IMPRINT",EDGE,{"disambiguationData":[TD([[subQ4,-1.0]])],"derivedFrom":subQ3}),1.0]])]});}
            var Q1;
            Q1=makeQuery(id+"F3.imprint","IMPRINT",FACE,{"disambiguationData":[TD([[makeQuery(id+"F3.imprint","IMPRINT",EDGE,{"derivedFrom":sQuery(id+"F3.wireOp",EDGE,"E12")}),1.0]])]});
            loft(context, id + "F4", {"sheetProfilesArray" : [{ "sheetProfileEntities" : qUnion([Q0]) }, { "sheetProfileEntities" : qUnion([Q1]) }]});
        }
        {
            var Q0;
            {var subQ5=sQuery(id+"F0.wireOp",EDGE,"E4");var subQ6=sQuery(id+"F0.wireOp",EDGE,"E3");var subQ7=makeQuery(id+"F0.imprint","INTERSECT",VERTEX,{"derivedFrom":[subQ6,subQ5]});Q0=makeQuery(id+"F0.imprint","IMPRINT",FACE,{"disambiguationData":[TD([[makeQuery(id+"F0.imprint","IMPRINT",EDGE,{"disambiguationData":[TD([[subQ7,1.0]])],"derivedFrom":subQ6}),-1.0]])]});}
            var Q1;
            Q1=makeQuery(id+"F3.imprint","IMPRINT",FACE,{"disambiguationData":[TD([[makeQuery(id+"F3.imprint","IMPRINT",EDGE,{"derivedFrom":sQuery(id+"F3.wireOp",EDGE,"E16.31.0")}),1.0]])]});
            loft(context, id + "F5", {"sheetProfilesArray" : [{ "sheetProfileEntities" : qUnion([Q0]) }, { "sheetProfileEntities" : qUnion([Q1]) }]});
        }
        {
            var Q0;
            {var subQ0=sQuery(id+"F0.wireOp",EDGE,"E10.1.3");var subQ3=sQuery(id+"F0.wireOp",EDGE,"E3");var subQ4=makeQuery(id+"F0.imprint","INTERSECT",VERTEX,{"derivedFrom":[subQ3,subQ0]});Q0=makeQuery(id+"F4.opLoft","SWEPT_BODY",BODY,{"disambiguationData":[OSD([makeQuery(id+"F0.imprint","IMPRINT",FACE,{"disambiguationData":[TD([[makeQuery(id+"F0.imprint","IMPRINT",EDGE,{"disambiguationData":[TD([[subQ4,-1.0]])],"derivedFrom":subQ3}),1.0]])]}),makeQuery(id+"F3.imprint","IMPRINT",FACE,{"disambiguationData":[TD([[makeQuery(id+"F3.imprint","IMPRINT",EDGE,{"derivedFrom":sQuery(id+"F3.wireOp",EDGE,"E12")}),1.0]])]})])]});}
            transform(context, id + "F6", {"entities" : qUnion([Q0]), "transformType" : TransformType.TRANSLATION_3D, "dx" : 0 * mm, "dy" : 0 * mm, "dz" : 0 * mm, "makeCopy" : true});
        }
        {
            var Q0;
            {var subQ0=sQuery(id+"F0.wireOp",EDGE,"E10.1.3");var subQ3=sQuery(id+"F0.wireOp",EDGE,"E3");var subQ4=makeQuery(id+"F0.imprint","INTERSECT",VERTEX,{"derivedFrom":[subQ3,subQ0]});Q0=makeQuery(id+"F6.opPattern","COPY",BODY,{"derivedFrom":makeQuery(id+"F4.opLoft","SWEPT_BODY",BODY,{"disambiguationData":[OSD([makeQuery(id+"F0.imprint","IMPRINT",FACE,{"disambiguationData":[TD([[makeQuery(id+"F0.imprint","IMPRINT",EDGE,{"disambiguationData":[TD([[subQ4,-1.0]])],"derivedFrom":subQ3}),1.0]])]}),makeQuery(id+"F3.imprint","IMPRINT",FACE,{"disambiguationData":[TD([[makeQuery(id+"F3.imprint","IMPRINT",EDGE,{"derivedFrom":sQuery(id+"F3.wireOp",EDGE,"E12")}),1.0]])]})])]}),"instanceName":"1"});}
            deleteBodies(context, id + "F7", {"entities" : qUnion([Q0])});
        }
    });
